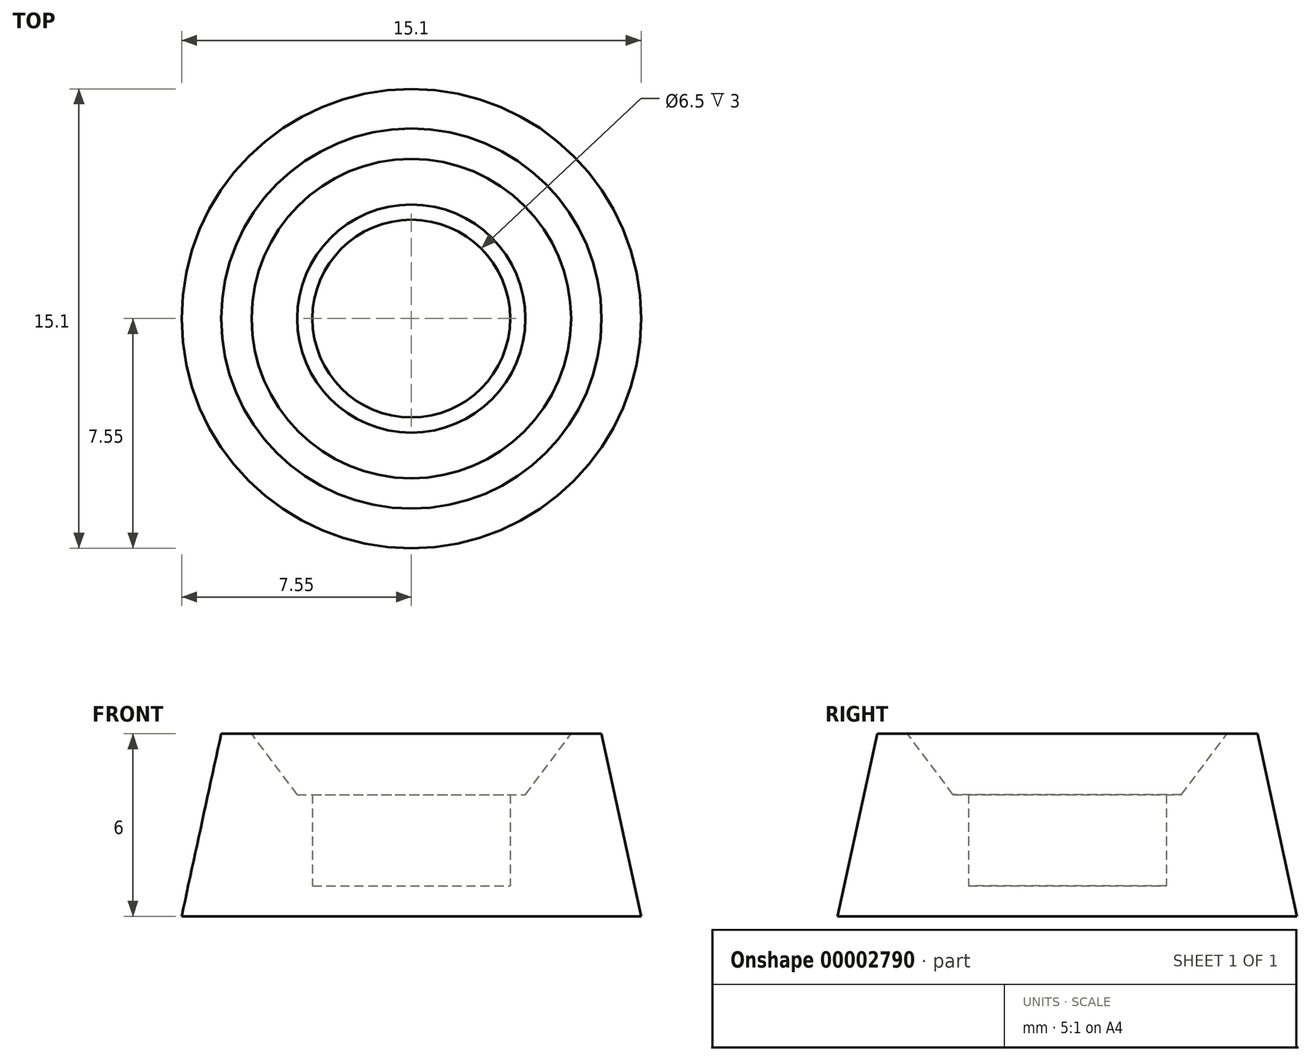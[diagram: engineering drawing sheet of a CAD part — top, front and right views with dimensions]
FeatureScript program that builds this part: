
annotation { "Feature Type Name" : "Feature", "Feature Type Description" : "" }
export const myFeature = defineFeature(function(context is Context, id is Id, definition is map)
    precondition{}
    {
        {
            var Q0;
            Q0=qCreatedBy(makeId("Front.planeOp"),FACE);
            var sketch = newSketch(context, id + "F0", { "sketchPlane" : qUnion([Q0])});
            skLineSegment(sketch, "E0", {"start": v(0, 0) * mm, "end": v(-7.55, 0) * mm, "construction": true});
            skLineSegment(sketch, "E1.0", {"start": v(-3.25, 4) * mm, "end": v(-3.25, 1) * mm});
            skLineSegment(sketch, "E2", {"start": v(0, 0) * mm, "end": v(-7.55, 0) * mm});
            skLineSegment(sketch, "E3.0", {"start": v(-3.25, 4) * mm, "end": v(-3.75, 4) * mm});
            skLineSegment(sketch, "E4.0", {"start": v(-6.25, 6) * mm, "end": v(-7.55, 0) * mm});
            skLineSegment(sketch, "E5.0", {"start": v(0, 1) * mm, "end": v(-3.25, 1) * mm});
            skLineSegment(sketch, "E6", {"start": v(-5.25, 6) * mm, "end": v(-3.75, 4) * mm});
            skLineSegment(sketch, "E7.trimOffspring", {"start": v(-5.25, 6) * mm, "end": v(-6.25, 6) * mm});
            skLineSegment(sketch, "E8", {"start": v(0, 0) * mm, "end": v(0, 1) * mm});
            skSolve(sketch);
        }
        {
            var Q0;
            Q0=makeQuery(id+"F0.imprint","IMPRINT",FACE,{"disambiguationData":[TD([[makeQuery(id+"F0.imprint","IMPRINT",EDGE,{"derivedFrom":sQuery(id+"F0.wireOp",EDGE,"E1.0")}),-1.0]])]});
            var Q1;
            Q1=sQuery(id+"F0.wireOp",EDGE,"E8");
            revolve(context, id + "F1", {"entities" : qUnion([Q0]), "axis" : qUnion([Q1]), "revolveType" : RevolveType.FULL});
        }
        {
            var Q0;
            Q0=makeQuery(id+"F1.opRevolve","SWEPT_FACE",FACE,{"disambiguationData":[OSD([sQuery(id+"F0.wireOp",EDGE,"E5.0")])]});
            var sketch = newSketch(context, id + "F2", { "sketchPlane" : qUnion([Q0])});
            skCircle(sketch, "E9", {"center": v(0, 0) * mm, "radius": 3 * mm});
            skSolve(sketch);
        }
        {
            var Q0;
            Q0 = qSketchRegion(id + "F2", true);
            extrude(context, id + "F3", {"entities" : qUnion([Q0]), "depth" : 3 * mm});
        }
        {
            var Q0;
            Q0=makeQuery(id+"F3.opExtrude","SWEPT_BODY",BODY,{"disambiguationData":[OSD([sQuery(id+"F2.wireOp",EDGE,"E9")])]});
            deleteBodies(context, id + "F4", {"entities" : qUnion([Q0])});
        }
    });
